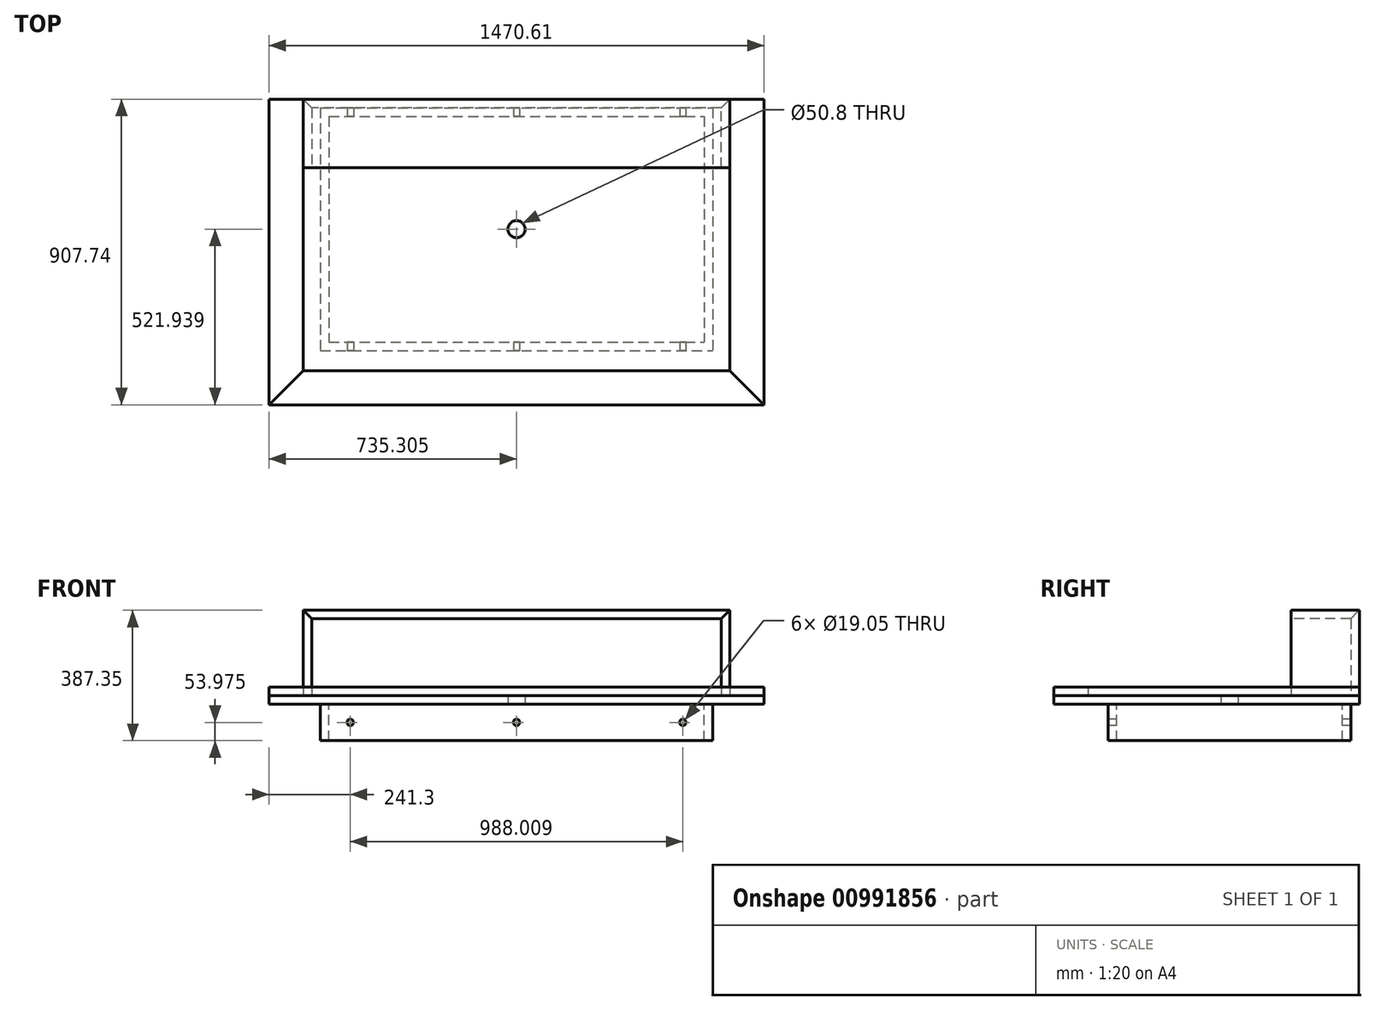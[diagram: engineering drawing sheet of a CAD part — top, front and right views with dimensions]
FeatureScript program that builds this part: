
annotation { "Feature Type Name" : "Feature", "Feature Type Description" : "" }
export const myFeature = defineFeature(function(context is Context, id is Id, definition is map)
    precondition{}
    {
        {
            var Q0;
            Q0=qCreatedBy(makeId("Top.planeOp"),FACE);
            var sketch = newSketch(context, id + "F0", { "sketchPlane" : qUnion([Q0])});
            skLineSegment(sketch, "E0.bottom", {"start": v(0, 0) * mm, "end": v(1470.6, 0) * mm});
            skLineSegment(sketch, "E0.top", {"start": v(0, -907.74) * mm, "end": v(1470.6, -907.74) * mm});
            skLineSegment(sketch, "E0.left", {"start": v(0, 0) * mm, "end": v(0, -907.74) * mm});
            skLineSegment(sketch, "E0.right", {"start": v(1470.6, 0) * mm, "end": v(1470.6, -907.74) * mm});
            skSolve(sketch);
        }
        {
            var Q0;
            Q0 = qSketchRegion(id + "F0", true);
            extrude(context, id + "F1", {"entities" : qUnion([Q0]), "depth" : 25.4 * mm, "offsetDistance" : 25.4 * mm});
        }
        {
            var Q0;
            Q0=makeQuery(id+"F1.opExtrude","CAP_FACE",FACE,{"disambiguationData":[OSD([sQuery(id+"F0.wireOp",EDGE,"E0.bottom"),sQuery(id+"F0.wireOp",EDGE,"E0.top"),sQuery(id+"F0.wireOp",EDGE,"E0.left"),sQuery(id+"F0.wireOp",EDGE,"E0.right")])],"isStart":true});
            var sketch = newSketch(context, id + "F2", { "sketchPlane" : qUnion([Q0])});
            skLineSegment(sketch, "E1.bottom", {"start": v(152.4, 25.4) * mm, "end": v(1318.2, 25.4) * mm});
            skLineSegment(sketch, "E1.top", {"start": v(152.4, 746.2) * mm, "end": v(1318.2, 746.2) * mm});
            skLineSegment(sketch, "E1.left", {"start": v(152.4, 25.4) * mm, "end": v(152.4, 746.2) * mm});
            skLineSegment(sketch, "E1.right", {"start": v(1318.2, 25.4) * mm, "end": v(1318.2, 746.2) * mm});
            skLineSegment(sketch, "E2.0", {"start": v(177.8, 720.8) * mm, "end": v(1292.8, 720.8) * mm});
            skLineSegment(sketch, "E2.1", {"start": v(177.8, 50.8) * mm, "end": v(177.8, 720.8) * mm});
            skLineSegment(sketch, "E2.2", {"start": v(177.8, 50.8) * mm, "end": v(1292.8, 50.8) * mm});
            skLineSegment(sketch, "E2.3", {"start": v(1292.8, 50.8) * mm, "end": v(1292.8, 720.8) * mm});
            skLineSegment(sketch, "E3", {"start": v(735.3, 0) * mm, "end": v(735.3, 25.4) * mm, "construction": true});
            skSolve(sketch);
        }
        {
            var Q0;
            Q0 = qSketchRegion(id + "F2", true);
            extrude(context, id + "F3", {"entities" : qUnion([Q0]), "operationType" : NewBodyOperationType.ADD, "depth" : 107.95 * mm, "offsetDistance" : 25.4 * mm});
        }
        {
            var Q0;
            Q0=makeQuery(id+"F3.boolean.opBoolean","SPLIT",FACE,{"disambiguationData":[TD([makeQuery(id+"F3.opExtrude","SWEPT_FACE",FACE,{"disambiguationData":[OSD([sQuery(id+"F2.wireOp",EDGE,"E2.0")])]})])],"derivedFrom":makeQuery(id+"F1.opExtrude","CAP_FACE",FACE,{"disambiguationData":[OSD([sQuery(id+"F0.wireOp",EDGE,"E0.bottom"),sQuery(id+"F0.wireOp",EDGE,"E0.top"),sQuery(id+"F0.wireOp",EDGE,"E0.left"),sQuery(id+"F0.wireOp",EDGE,"E0.right")])],"isStart":true})});
            var sketch = newSketch(context, id + "F4", { "sketchPlane" : qUnion([Q0])});
            skLineSegment(sketch, "E4", {"start": v(177.8, 385.8) * mm, "end": v(735.3, 385.8) * mm, "construction": true});
            skLineSegment(sketch, "E5", {"start": v(735.3, 385.8) * mm, "end": v(735.3, 720.8) * mm, "construction": true});
            skCircle(sketch, "E6", {"center": v(735.3, 385.8) * mm, "radius": 25.4 * mm});
            skSolve(sketch);
        }
        {
            var Q0;
            Q0=makeQuery(id+"F4.imprint","IMPRINT",FACE,{"disambiguationData":[TD([[makeQuery(id+"F4.imprint","IMPRINT",EDGE,{"derivedFrom":sQuery(id+"F4.wireOp",EDGE,"E6")}),1.0]])]});
            var Q1;
            Q1=makeQuery(id+"F1.opExtrude","CAP_FACE",FACE,{"disambiguationData":[OSD([sQuery(id+"F0.wireOp",EDGE,"E0.bottom"),sQuery(id+"F0.wireOp",EDGE,"E0.top"),sQuery(id+"F0.wireOp",EDGE,"E0.left"),sQuery(id+"F0.wireOp",EDGE,"E0.right")])],"isStart":false});
            var Q2;
            Q2=makeQuery(id+"F1.opExtrude","CAP_VERTEX",VERTEX,{"disambiguationData":[OSD([sQuery(id+"F0.wireOp",EDGE,"E0.bottom"),sQuery(id+"F0.wireOp",EDGE,"E0.left")])],"isStart":false});
            extrude(context, id + "F5", {"entities" : qUnion([Q0]), "operationType" : NewBodyOperationType.REMOVE, "endBound" : BoundingType.UP_TO_SURFACE, "oppositeDirection" : true, "depth" : 25.4 * mm, "endBoundEntityFace" : qUnion([Q1]), "endBoundEntityVertex" : qUnion([Q2]), "offsetDistance" : 25.4 * mm});
        }
        {
            var Q0;
            Q0=makeQuery(id+"F3.opExtrude","SWEPT_FACE",FACE,{"disambiguationData":[OSD([sQuery(id+"F2.wireOp",EDGE,"E1.top")])]});
            var sketch = newSketch(context, id + "F6", { "sketchPlane" : qUnion([Q0])});
            skLineSegment(sketch, "E7", {"start": v(152.4, -53.98) * mm, "end": v(241.3, -53.98) * mm, "construction": true});
            skLineSegment(sketch, "E8", {"start": v(241.3, -53.98) * mm, "end": v(735.3, -53.98) * mm, "construction": true});
            skLineSegment(sketch, "E9", {"start": v(735.3, -53.98) * mm, "end": v(1229.3, -53.98) * mm, "construction": true});
            skLineSegment(sketch, "E10", {"start": v(1229.3, -53.98) * mm, "end": v(1318.2, -53.98) * mm, "construction": true});
            skLineSegment(sketch, "E11", {"start": v(735.3, -53.97) * mm, "end": v(735.3, -107.95) * mm, "construction": true});
            skCircle(sketch, "E12", {"center": v(735.3, -53.98) * mm, "radius": 9.53 * mm});
            skCircle(sketch, "E13", {"center": v(241.3, -53.98) * mm, "radius": 9.53 * mm});
            skCircle(sketch, "E14", {"center": v(1229.3, -53.97) * mm, "radius": 9.53 * mm});
            skSolve(sketch);
        }
        {
            var Q0;
            Q0 = qSketchRegion(id + "F6", true);
            var Q1;
            Q1=makeQuery(id+"F3.opExtrude","SWEPT_FACE",FACE,{"disambiguationData":[OSD([sQuery(id+"F2.wireOp",EDGE,"E1.bottom")])]});
            extrude(context, id + "F7", {"entities" : qUnion([Q0]), "operationType" : NewBodyOperationType.REMOVE, "endBound" : BoundingType.UP_TO_SURFACE, "oppositeDirection" : true, "depth" : 25.4 * mm, "endBoundEntityFace" : qUnion([Q1]), "offsetDistance" : 25.4 * mm});
        }
        {
            var Q0;
            Q0=makeQuery(id+"F1.opExtrude","CAP_FACE",FACE,{"disambiguationData":[OSD([sQuery(id+"F0.wireOp",EDGE,"E0.bottom"),sQuery(id+"F0.wireOp",EDGE,"E0.top"),sQuery(id+"F0.wireOp",EDGE,"E0.left"),sQuery(id+"F0.wireOp",EDGE,"E0.right")])],"isStart":false});
            var sketch = newSketch(context, id + "F8", { "sketchPlane" : qUnion([Q0])});
            skLineSegment(sketch, "E15", {"start": v(0, 0) * mm, "end": v(0, -907.74) * mm});
            skLineSegment(sketch, "E16", {"start": v(0, -907.74) * mm, "end": v(101.6, -806.14) * mm});
            skLineSegment(sketch, "E17", {"start": v(101.6, -806.14) * mm, "end": v(101.6, 0) * mm});
            skLineSegment(sketch, "E18", {"start": v(101.6, 0) * mm, "end": v(0, 0) * mm});
            skLineSegment(sketch, "E19", {"start": v(0, -907.74) * mm, "end": v(1470.6, -907.74) * mm});
            skLineSegment(sketch, "E20", {"start": v(1470.6, -907.74) * mm, "end": v(1470.6, 0) * mm});
            skLineSegment(sketch, "E21", {"start": v(1470.6, 0) * mm, "end": v(1369, 0) * mm});
            skLineSegment(sketch, "E22", {"start": v(1369, 0) * mm, "end": v(1369, -806.14) * mm});
            skLineSegment(sketch, "E23", {"start": v(1369, -806.14) * mm, "end": v(1470.6, -907.74) * mm});
            skLineSegment(sketch, "E24", {"start": v(1369, -806.14) * mm, "end": v(101.6, -806.14) * mm});
            skSolve(sketch);
        }
        {
            var Q0;
            Q0=makeQuery(id+"F8.imprint","IMPRINT",FACE,{"disambiguationData":[TD([[makeQuery(id+"F8.imprint","IMPRINT",EDGE,{"derivedFrom":sQuery(id+"F8.wireOp",EDGE,"E15")}),1.0]])]});
            extrude(context, id + "F9", {"entities" : qUnion([Q0]), "depth" : 25.4 * mm, "offsetDistance" : 25.4 * mm});
        }
        {
            var Q0;
            Q0=makeQuery(id+"F8.imprint","IMPRINT",FACE,{"disambiguationData":[TD([[makeQuery(id+"F8.imprint","IMPRINT",EDGE,{"derivedFrom":sQuery(id+"F8.wireOp",EDGE,"E16")}),-1.0]])]});
            extrude(context, id + "F10", {"entities" : qUnion([Q0]), "depth" : 25.4 * mm, "offsetDistance" : 25.4 * mm});
        }
        {
            var Q0;
            Q0=makeQuery(id+"F8.imprint","IMPRINT",FACE,{"disambiguationData":[TD([[makeQuery(id+"F8.imprint","IMPRINT",EDGE,{"derivedFrom":sQuery(id+"F8.wireOp",EDGE,"E20")}),-1.0]])]});
            extrude(context, id + "F11", {"entities" : qUnion([Q0]), "depth" : 25.4 * mm, "offsetDistance" : 25.4 * mm});
        }
        {
            var Q0;
            Q0=makeQuery(id+"F1.opExtrude","CAP_FACE",FACE,{"disambiguationData":[OSD([sQuery(id+"F0.wireOp",EDGE,"E0.bottom"),sQuery(id+"F0.wireOp",EDGE,"E0.top"),sQuery(id+"F0.wireOp",EDGE,"E0.left"),sQuery(id+"F0.wireOp",EDGE,"E0.right")])],"isStart":false});
            var sketch = newSketch(context, id + "F12", { "sketchPlane" : qUnion([Q0])});
            skLineSegment(sketch, "E25.bottom", {"start": v(101.6, 0) * mm, "end": v(127, 0) * mm});
            skLineSegment(sketch, "E25.top", {"start": v(101.6, -203.2) * mm, "end": v(127, -203.2) * mm});
            skLineSegment(sketch, "E25.left", {"start": v(101.6, 0) * mm, "end": v(101.6, -203.2) * mm});
            skLineSegment(sketch, "E25.right", {"start": v(127, 0) * mm, "end": v(127, -203.2) * mm});
            skLineSegment(sketch, "E26.bottom", {"start": v(1343.6, 0) * mm, "end": v(1369, 0) * mm});
            skLineSegment(sketch, "E26.top", {"start": v(1343.6, -203.2) * mm, "end": v(1369, -203.2) * mm});
            skLineSegment(sketch, "E26.left", {"start": v(1343.6, 0) * mm, "end": v(1343.6, -203.2) * mm});
            skLineSegment(sketch, "E26.right", {"start": v(1369, 0) * mm, "end": v(1369, -203.2) * mm});
            skLineSegment(sketch, "E27", {"start": v(735.3, -385.8) * mm, "end": v(735.3, -101.6) * mm, "construction": true});
            skLineSegment(sketch, "E28", {"start": v(735.3, -101.6) * mm, "end": v(127, -101.6) * mm, "construction": true});
            skLineSegment(sketch, "E29", {"start": v(1343.6, -101.6) * mm, "end": v(735.3, -101.6) * mm, "construction": true});
            skLineSegment(sketch, "E30.bottom", {"start": v(127, 0) * mm, "end": v(1343.6, 0) * mm});
            skLineSegment(sketch, "E30.top", {"start": v(127, -25.4) * mm, "end": v(1343.6, -25.4) * mm});
            skLineSegment(sketch, "E30.left", {"start": v(127, 0) * mm, "end": v(127, -25.4) * mm});
            skLineSegment(sketch, "E30.right", {"start": v(1343.6, 0) * mm, "end": v(1343.6, -25.4) * mm});
            skSolve(sketch);
        }
        {
            var Q0;
            Q0 = qSketchRegion(id + "F12", true);
            extrude(context, id + "F13", {"entities" : qUnion([Q0]), "depth" : 254 * mm, "offsetDistance" : 25.4 * mm});
        }
        {
            var Q0;
            Q0=makeQuery(id+"F13.opExtrude","CAP_EDGE",EDGE,{"disambiguationData":[OSD([sQuery(id+"F12.wireOp",EDGE,"E30.top")])],"isStart":false});
            var Q1;
            Q1=makeQuery(id+"F13.opExtrude","CAP_EDGE",EDGE,{"disambiguationData":[OSD([sQuery(id+"F12.wireOp",EDGE,"E25.right")])],"isStart":false});
            var Q2;
            Q2=makeQuery(id+"F13.opExtrude","CAP_EDGE",EDGE,{"disambiguationData":[OSD([sQuery(id+"F12.wireOp",EDGE,"E26.left")])],"isStart":false});
            chamfer(context, id + "F14", {"entities" : qUnion([Q0, Q1, Q2]), "width" : 25.4 * mm, "tangentPropagation" : true});
        }
        {
            var Q0;
            Q0=makeQuery(id+"F14.opChamfer","BLEND_VERTEX",VERTEX,{"blendedFrom":[makeQuery(id+"F13.opExtrude","CAP_EDGE",EDGE,{"disambiguationData":[OSD([sQuery(id+"F12.wireOp",EDGE,"E25.right")])],"isStart":false}),makeQuery(id+"F13.opExtrude","SWEPT_FACE",FACE,{"disambiguationData":[OSD([sQuery(id+"F12.wireOp",EDGE,"E25.top")])]}),makeQuery(id+"F13.opExtrude","SWEPT_FACE",FACE,{"disambiguationData":[OSD([sQuery(id+"F12.wireOp",EDGE,"E25.left")])]})],"blendedInto":[makeQuery(id+"F13.opExtrude","SWEPT_FACE",FACE,{"disambiguationData":[OSD([sQuery(id+"F12.wireOp",EDGE,"E25.top")])]}),makeQuery(id+"F13.opExtrude","SWEPT_FACE",FACE,{"disambiguationData":[OSD([sQuery(id+"F12.wireOp",EDGE,"E25.left")])]})]});
            var Q1;
            Q1=makeQuery(id+"F14.opChamfer","BLEND_VERTEX",VERTEX,{"blendedFrom":[makeQuery(id+"F13.opExtrude","CAP_EDGE",EDGE,{"disambiguationData":[OSD([sQuery(id+"F12.wireOp",EDGE,"E25.right")])],"isStart":false}),makeQuery(id+"F13.opExtrude","CAP_EDGE",EDGE,{"disambiguationData":[OSD([sQuery(id+"F12.wireOp",EDGE,"E30.top")])],"isStart":false}),makeQuery(id+"F13.opExtrude","SWEPT_FACE",FACE,{"disambiguationData":[OSD([sQuery(id+"F12.wireOp",EDGE,"E25.bottom"),sQuery(id+"F12.wireOp",EDGE,"E26.bottom"),sQuery(id+"F12.wireOp",EDGE,"E30.bottom")])]}),makeQuery(id+"F13.opExtrude","SWEPT_FACE",FACE,{"disambiguationData":[OSD([sQuery(id+"F12.wireOp",EDGE,"E25.left")])]})],"blendedInto":[makeQuery(id+"F13.opExtrude","SWEPT_FACE",FACE,{"disambiguationData":[OSD([sQuery(id+"F12.wireOp",EDGE,"E25.bottom"),sQuery(id+"F12.wireOp",EDGE,"E26.bottom"),sQuery(id+"F12.wireOp",EDGE,"E30.bottom")])]}),makeQuery(id+"F13.opExtrude","SWEPT_FACE",FACE,{"disambiguationData":[OSD([sQuery(id+"F12.wireOp",EDGE,"E25.left")])]})]});
            var Q2;
            Q2=makeQuery(id+"F14.opChamfer","BLEND_VERTEX",VERTEX,{"blendedFrom":[makeQuery(id+"F13.opExtrude","CAP_EDGE",EDGE,{"disambiguationData":[OSD([sQuery(id+"F12.wireOp",EDGE,"E26.left")])],"isStart":false}),makeQuery(id+"F13.opExtrude","SWEPT_FACE",FACE,{"disambiguationData":[OSD([sQuery(id+"F12.wireOp",EDGE,"E26.top")])]}),makeQuery(id+"F13.opExtrude","SWEPT_FACE",FACE,{"disambiguationData":[OSD([sQuery(id+"F12.wireOp",EDGE,"E26.right")])]})],"blendedInto":[makeQuery(id+"F13.opExtrude","SWEPT_FACE",FACE,{"disambiguationData":[OSD([sQuery(id+"F12.wireOp",EDGE,"E26.top")])]}),makeQuery(id+"F13.opExtrude","SWEPT_FACE",FACE,{"disambiguationData":[OSD([sQuery(id+"F12.wireOp",EDGE,"E26.right")])]})]});
            cPlane(context, id + "F15", {"entities" : qUnion([Q0, Q1, Q2]), "cplaneType" : CPlaneType.THREE_POINT, "offset" : 25.4 * mm, "width" : 152.4 * mm, "height" : 152.4 * mm});
        }
        {
            var Q0;
            Q0=qCreatedBy(id+"F15.planeOp",FACE);
            var sketch = newSketch(context, id + "F16", { "sketchPlane" : qUnion([Q0])});
            skLineSegment(sketch, "E31.bottom", {"start": v(101.6, -203.2) * mm, "end": v(1369, -203.2) * mm});
            skLineSegment(sketch, "E31.top", {"start": v(101.6, 0) * mm, "end": v(1369, 0) * mm});
            skLineSegment(sketch, "E31.left", {"start": v(101.6, -203.2) * mm, "end": v(101.6, 0) * mm});
            skLineSegment(sketch, "E31.right", {"start": v(1369, -203.2) * mm, "end": v(1369, 0) * mm});
            skSolve(sketch);
        }
        {
            var Q0;
            Q0 = qSketchRegion(id + "F16", true);
            extrude(context, id + "F17", {"entities" : qUnion([Q0]), "oppositeDirection" : true, "depth" : 25.4 * mm, "offsetDistance" : 25.4 * mm});
        }
        {
            var Q0;
            Q0=makeQuery(id+"F17.opExtrude","CAP_EDGE",EDGE,{"disambiguationData":[OSD([sQuery(id+"F16.wireOp",EDGE,"E31.left")])],"isStart":false});
            var Q1;
            Q1=makeQuery(id+"F17.opExtrude","CAP_EDGE",EDGE,{"disambiguationData":[OSD([sQuery(id+"F16.wireOp",EDGE,"E31.top")])],"isStart":false});
            var Q2;
            Q2=makeQuery(id+"F17.opExtrude","CAP_EDGE",EDGE,{"disambiguationData":[OSD([sQuery(id+"F16.wireOp",EDGE,"E31.right")])],"isStart":false});
            chamfer(context, id + "F18", {"entities" : qUnion([Q0, Q1, Q2]), "width" : 25.4 * mm, "tangentPropagation" : true});
        }
    });
